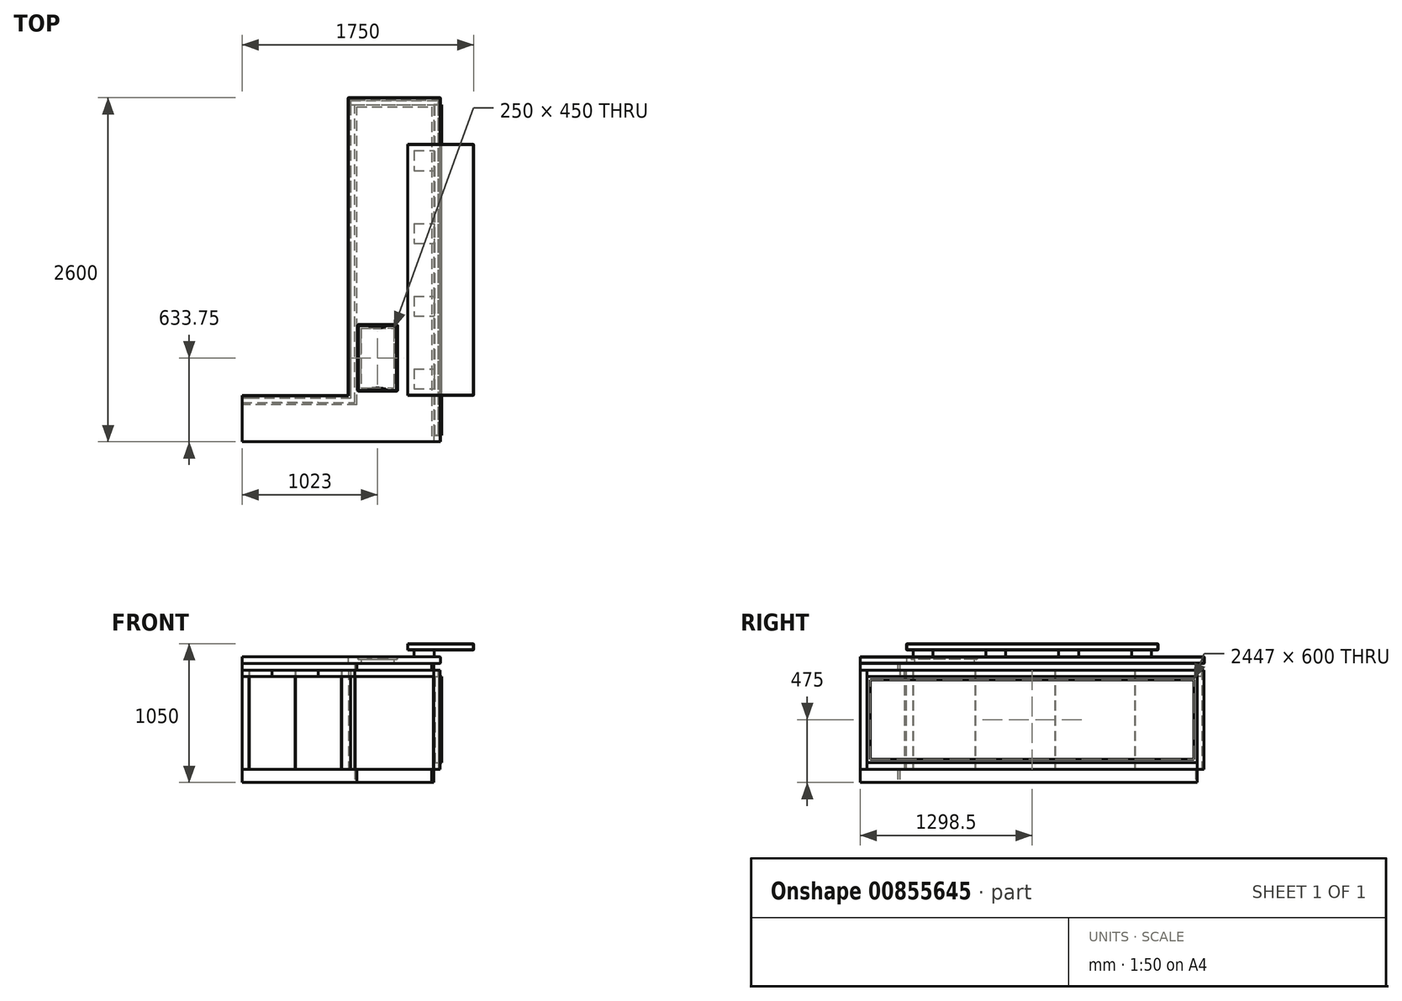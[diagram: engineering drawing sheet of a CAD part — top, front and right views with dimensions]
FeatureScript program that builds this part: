
annotation { "Feature Type Name" : "Feature", "Feature Type Description" : "" }
export const myFeature = defineFeature(function(context is Context, id is Id, definition is map)
    precondition{}
    {
        {
            var Q0;
            Q0=qCreatedBy(makeId("Top.planeOp"),FACE);
            var sketch = newSketch(context, id + "F0", { "sketchPlane" : qUnion([Q0])});
            skLineSegment(sketch, "E0", {"start": v(0, 0) * mm, "end": v(1500, 0) * mm});
            skLineSegment(sketch, "E1", {"start": v(1500, 0) * mm, "end": v(1500, 2600) * mm});
            skLineSegment(sketch, "E2", {"start": v(1500, 2600) * mm, "end": v(800, 2600) * mm});
            skLineSegment(sketch, "E3", {"start": v(800, 2600) * mm, "end": v(800, 350) * mm});
            skLineSegment(sketch, "E4", {"start": v(800, 350) * mm, "end": v(0, 350) * mm});
            skLineSegment(sketch, "E5", {"start": v(0, 350) * mm, "end": v(0, 0) * mm});
            skLineSegment(sketch, "E6.bottom", {"start": v(225, 300) * mm, "end": v(575, 300) * mm});
            skLineSegment(sketch, "E6.top", {"start": v(225, 50) * mm, "end": v(575, 50) * mm});
            skLineSegment(sketch, "E6.left", {"start": v(225, 300) * mm, "end": v(225, 50) * mm});
            skLineSegment(sketch, "E6.right", {"start": v(575, 300) * mm, "end": v(575, 50) * mm});
            skLineSegment(sketch, "E7", {"start": v(400, 350) * mm, "end": v(400, 300) * mm, "construction": true});
            skLineSegment(sketch, "E8", {"start": v(400, 50) * mm, "end": v(400, 0) * mm, "construction": true});
            skSolve(sketch);
        }
        {
            var Q0;
            Q0=makeQuery(id+"F0.imprint","IMPRINT",FACE,{"disambiguationData":[TD([[makeQuery(id+"F0.imprint","IMPRINT",EDGE,{"derivedFrom":sQuery(id+"F0.wireOp",EDGE,"E0")}),1.0]])]});
            var Q1;
            Q1=makeQuery(id+"F0.imprint","IMPRINT",FACE,{"disambiguationData":[TD([[makeQuery(id+"F0.imprint","IMPRINT",EDGE,{"derivedFrom":sQuery(id+"F0.wireOp",EDGE,"E6.bottom")}),-1.0]])]});
            extrude(context, id + "F1", {"entities" : qUnion([Q0, Q1]), "depth" : 950 * mm, "offsetDistance" : 25 * mm, "hasSecondDirection" : true, "secondDirectionOppositeDirection" : false, "secondDirectionDepth" : 900 * mm});
        }
        {
            var Q0;
            Q0=makeQuery(id+"F1.opExtrude","CAP_FACE",FACE,{"disambiguationData":[OSD([sQuery(id+"F0.wireOp",EDGE,"E0"),sQuery(id+"F0.wireOp",EDGE,"E1"),sQuery(id+"F0.wireOp",EDGE,"E2"),sQuery(id+"F0.wireOp",EDGE,"E3"),sQuery(id+"F0.wireOp",EDGE,"E4"),sQuery(id+"F0.wireOp",EDGE,"E5"),sQuery(id+"F0.wireOp",EDGE,"E6.bottom"),sQuery(id+"F0.wireOp",EDGE,"E6.top"),sQuery(id+"F0.wireOp",EDGE,"E6.left"),sQuery(id+"F0.wireOp",EDGE,"E6.right")])],"isStart":false});
            var sketch = newSketch(context, id + "F2", { "sketchPlane" : qUnion([Q0])});
            skLineSegment(sketch, "E9.bottom", {"start": v(1250, 2250) * mm, "end": v(1750, 2250) * mm});
            skLineSegment(sketch, "E9.top", {"start": v(1250, 350) * mm, "end": v(1750, 350) * mm});
            skLineSegment(sketch, "E9.left", {"start": v(1250, 2250) * mm, "end": v(1250, 350) * mm});
            skLineSegment(sketch, "E9.right", {"start": v(1750, 2250) * mm, "end": v(1750, 350) * mm});
            skLineSegment(sketch, "E10", {"start": v(1500, 2600) * mm, "end": v(1500, 2250) * mm, "construction": true});
            skLineSegment(sketch, "E11", {"start": v(1500, 0) * mm, "end": v(1500, 350) * mm, "construction": true});
            skLineSegment(sketch, "E12", {"start": v(800, 350) * mm, "end": v(1250, 350) * mm, "construction": true});
            skLineSegment(sketch, "E13.bottom", {"start": v(1300, 2200) * mm, "end": v(1450, 2200) * mm});
            skLineSegment(sketch, "E13.top", {"start": v(1300, 2050) * mm, "end": v(1450, 2050) * mm});
            skLineSegment(sketch, "E13.left", {"start": v(1300, 2200) * mm, "end": v(1300, 2050) * mm});
            skLineSegment(sketch, "E13.right", {"start": v(1450, 2200) * mm, "end": v(1450, 2050) * mm});
            skLineSegment(sketch, "E14.bottom", {"start": v(1300, 550) * mm, "end": v(1450, 550) * mm});
            skLineSegment(sketch, "E14.top", {"start": v(1300, 400) * mm, "end": v(1450, 400) * mm});
            skLineSegment(sketch, "E14.left", {"start": v(1300, 550) * mm, "end": v(1300, 400) * mm});
            skLineSegment(sketch, "E14.right", {"start": v(1450, 550) * mm, "end": v(1450, 400) * mm});
            skLineSegment(sketch, "E15.bottom", {"start": v(1300, 1650) * mm, "end": v(1450, 1650) * mm});
            skLineSegment(sketch, "E15.top", {"start": v(1300, 1500) * mm, "end": v(1450, 1500) * mm});
            skLineSegment(sketch, "E15.left", {"start": v(1300, 1650) * mm, "end": v(1300, 1500) * mm});
            skLineSegment(sketch, "E15.right", {"start": v(1450, 1650) * mm, "end": v(1450, 1500) * mm});
            skLineSegment(sketch, "E16.bottom", {"start": v(1300, 1100) * mm, "end": v(1450, 1100) * mm});
            skLineSegment(sketch, "E16.top", {"start": v(1300, 950) * mm, "end": v(1450, 950) * mm});
            skLineSegment(sketch, "E16.left", {"start": v(1300, 1100) * mm, "end": v(1300, 950) * mm});
            skLineSegment(sketch, "E16.right", {"start": v(1450, 1100) * mm, "end": v(1450, 950) * mm});
            skLineSegment(sketch, "E17", {"start": v(1500, 2250) * mm, "end": v(1500, 350) * mm, "construction": true});
            skLineSegment(sketch, "E18", {"start": v(1300, 2125) * mm, "end": v(1250, 2125) * mm, "construction": true});
            skLineSegment(sketch, "E19", {"start": v(1450, 2125) * mm, "end": v(1500, 2125) * mm, "construction": true});
            skLineSegment(sketch, "E20", {"start": v(1375, 2200) * mm, "end": v(1375, 2250) * mm, "construction": true});
            skLineSegment(sketch, "E21", {"start": v(1375, 400) * mm, "end": v(1375, 350) * mm, "construction": true});
            skLineSegment(sketch, "E22", {"start": v(1375, 2050) * mm, "end": v(1375, 1650) * mm, "construction": true});
            skLineSegment(sketch, "E23", {"start": v(1375, 1500) * mm, "end": v(1375, 1100) * mm, "construction": true});
            skLineSegment(sketch, "E24", {"start": v(1375, 950) * mm, "end": v(1375, 550) * mm, "construction": true});
            skSolve(sketch);
        }
        {
            var Q0;
            {var subQ0=sQuery(id+"F2.wireOp",EDGE,"E9.right");Q0=makeQuery(id+"F2.imprint","IMPRINT",FACE,{"disambiguationData":[TD([[makeQuery(id+"F2.imprint","IMPRINT",EDGE,{"derivedFrom":subQ0}),-1.0]])]});}
            var Q1;
            {var subQ5=sQuery(id+"F2.wireOp",EDGE,"E9.left");Q1=makeQuery(id+"F2.imprint","IMPRINT",FACE,{"disambiguationData":[TD([[makeQuery(id+"F2.imprint","IMPRINT",EDGE,{"derivedFrom":subQ5}),1.0]])]});}
            var Q2;
            Q2=makeQuery(id+"F2.imprint","IMPRINT",FACE,{"disambiguationData":[TD([[makeQuery(id+"F2.imprint","IMPRINT",EDGE,{"derivedFrom":sQuery(id+"F2.wireOp",EDGE,"E13.bottom")}),-1.0]])]});
            var Q3;
            Q3=makeQuery(id+"F2.imprint","IMPRINT",FACE,{"disambiguationData":[TD([[makeQuery(id+"F2.imprint","IMPRINT",EDGE,{"derivedFrom":sQuery(id+"F2.wireOp",EDGE,"E15.bottom")}),-1.0]])]});
            var Q4;
            Q4=makeQuery(id+"F2.imprint","IMPRINT",FACE,{"disambiguationData":[TD([[makeQuery(id+"F2.imprint","IMPRINT",EDGE,{"derivedFrom":sQuery(id+"F2.wireOp",EDGE,"E16.bottom")}),-1.0]])]});
            var Q5;
            Q5=makeQuery(id+"F2.imprint","IMPRINT",FACE,{"disambiguationData":[TD([[makeQuery(id+"F2.imprint","IMPRINT",EDGE,{"derivedFrom":sQuery(id+"F2.wireOp",EDGE,"E14.bottom")}),-1.0]])]});
            extrude(context, id + "F3", {"entities" : qUnion([Q0, Q1, Q2, Q3, Q4, Q5]), "depth" : 100 * mm, "offsetDistance" : 25 * mm, "hasSecondDirection" : true, "secondDirectionOppositeDirection" : false, "secondDirectionDepth" : 50 * mm});
        }
        {
            var Q0;
            Q0=makeQuery(id+"F2.imprint","IMPRINT",FACE,{"disambiguationData":[TD([[makeQuery(id+"F2.imprint","IMPRINT",EDGE,{"derivedFrom":sQuery(id+"F2.wireOp",EDGE,"E15.bottom")}),-1.0]])]});
            var Q1;
            Q1=makeQuery(id+"F2.imprint","IMPRINT",FACE,{"disambiguationData":[TD([[makeQuery(id+"F2.imprint","IMPRINT",EDGE,{"derivedFrom":sQuery(id+"F2.wireOp",EDGE,"E13.bottom")}),-1.0]])]});
            var Q2;
            Q2=makeQuery(id+"F2.imprint","IMPRINT",FACE,{"disambiguationData":[TD([[makeQuery(id+"F2.imprint","IMPRINT",EDGE,{"derivedFrom":sQuery(id+"F2.wireOp",EDGE,"E16.bottom")}),-1.0]])]});
            var Q3;
            Q3=makeQuery(id+"F2.imprint","IMPRINT",FACE,{"disambiguationData":[TD([[makeQuery(id+"F2.imprint","IMPRINT",EDGE,{"derivedFrom":sQuery(id+"F2.wireOp",EDGE,"E14.bottom")}),-1.0]])]});
            extrude(context, id + "F4", {"entities" : qUnion([Q0, Q1, Q2, Q3]), "depth" : 50 * mm, "offsetDistance" : 25 * mm});
        }
        {
            var Q0;
            Q0=makeQuery(id+"F3.opExtrude","CAP_FACE",FACE,{"disambiguationData":[OSD([sQuery(id+"F2.wireOp",EDGE,"E9.bottom"),sQuery(id+"F2.wireOp",EDGE,"E9.top"),sQuery(id+"F2.wireOp",EDGE,"E9.left"),sQuery(id+"F2.wireOp",EDGE,"E9.right")])],"isStart":false});
            var Q1;
            Q1=makeQuery(id+"F3.opExtrude","CAP_FACE",FACE,{"disambiguationData":[OSD([sQuery(id+"F2.wireOp",EDGE,"E9.bottom"),sQuery(id+"F2.wireOp",EDGE,"E9.top"),sQuery(id+"F2.wireOp",EDGE,"E9.left"),sQuery(id+"F2.wireOp",EDGE,"E9.right")])],"isStart":true});
            var Q2;
            Q2=makeQuery(id+"F3.opExtrude","SWEPT_EDGE",EDGE,{"disambiguationData":[OSD([sQuery(id+"F2.wireOp",EDGE,"E9.bottom"),sQuery(id+"F2.wireOp",EDGE,"E9.right")])]});
            var Q3;
            Q3=makeQuery(id+"F1.opExtrude","SWEPT_EDGE",EDGE,{"disambiguationData":[OSD([sQuery(id+"F0.wireOp",EDGE,"E1"),sQuery(id+"F0.wireOp",EDGE,"E2")])]});
            var Q4;
            Q4=makeQuery(id+"F3.opExtrude","SWEPT_EDGE",EDGE,{"disambiguationData":[OSD([sQuery(id+"F2.wireOp",EDGE,"E9.bottom"),sQuery(id+"F2.wireOp",EDGE,"E9.left")])]});
            var Q5;
            Q5=makeQuery(id+"F3.opExtrude","SWEPT_EDGE",EDGE,{"disambiguationData":[OSD([sQuery(id+"F2.wireOp",EDGE,"E9.top"),sQuery(id+"F2.wireOp",EDGE,"E9.left")])]});
            var Q6;
            Q6=makeQuery(id+"F1.opExtrude","SWEPT_EDGE",EDGE,{"disambiguationData":[OSD([sQuery(id+"F0.wireOp",EDGE,"E2"),sQuery(id+"F0.wireOp",EDGE,"E3")])]});
            var Q7;
            Q7=makeQuery(id+"F3.opExtrude","SWEPT_EDGE",EDGE,{"disambiguationData":[OSD([sQuery(id+"F2.wireOp",EDGE,"E9.top"),sQuery(id+"F2.wireOp",EDGE,"E9.right")])]});
            var Q8;
            Q8=makeQuery(id+"F1.opExtrude","CAP_EDGE",EDGE,{"disambiguationData":[OSD([sQuery(id+"F0.wireOp",EDGE,"E4")])],"isStart":false});
            var Q9;
            Q9=makeQuery(id+"F1.opExtrude","CAP_EDGE",EDGE,{"disambiguationData":[OSD([sQuery(id+"F0.wireOp",EDGE,"E3")])],"isStart":true});
            var Q10;
            Q10=makeQuery(id+"F1.opExtrude","CAP_EDGE",EDGE,{"disambiguationData":[OSD([sQuery(id+"F0.wireOp",EDGE,"E3")])],"isStart":false});
            var Q11;
            Q11=makeQuery(id+"F1.opExtrude","CAP_EDGE",EDGE,{"disambiguationData":[OSD([sQuery(id+"F0.wireOp",EDGE,"E4")])],"isStart":true});
            var Q12;
            Q12=makeQuery(id+"F1.opExtrude","CAP_EDGE",EDGE,{"disambiguationData":[OSD([sQuery(id+"F0.wireOp",EDGE,"E2")])],"isStart":false});
            var Q13;
            Q13=makeQuery(id+"F1.opExtrude","CAP_EDGE",EDGE,{"disambiguationData":[OSD([sQuery(id+"F0.wireOp",EDGE,"E2")])],"isStart":true});
            var Q14;
            Q14=makeQuery(id+"F1.opExtrude","CAP_EDGE",EDGE,{"disambiguationData":[OSD([sQuery(id+"F0.wireOp",EDGE,"E1")])],"isStart":false});
            var Q15;
            Q15=makeQuery(id+"F1.opExtrude","CAP_EDGE",EDGE,{"disambiguationData":[OSD([sQuery(id+"F0.wireOp",EDGE,"E1")])],"isStart":true});
            chamfer(context, id + "F5", {"entities" : qUnion([Q0, Q1, Q2, Q3, Q4, Q5, Q6, Q7, Q8, Q9, Q10, Q11, Q12, Q13, Q14, Q15]), "width" : 3 * mm, "tangentPropagation" : true});
        }
        {
            var Q0;
            Q0=makeQuery(id+"F0.imprint","IMPRINT",FACE,{"disambiguationData":[TD([[makeQuery(id+"F0.imprint","IMPRINT",EDGE,{"derivedFrom":sQuery(id+"F0.wireOp",EDGE,"E0")}),1.0]])]});
            var sketch = newSketch(context, id + "F6", { "sketchPlane" : qUnion([Q0])});
            skLineSegment(sketch, "E25.bottom", {"start": v(0, 347) * mm, "end": v(50, 347) * mm});
            skLineSegment(sketch, "E25.top", {"start": v(0, 332) * mm, "end": v(50, 332) * mm});
            skLineSegment(sketch, "E25.left", {"start": v(0, 347) * mm, "end": v(0, 332) * mm});
            skLineSegment(sketch, "E25.right", {"start": v(50, 347) * mm, "end": v(50, 332) * mm});
            skLineSegment(sketch, "E26.bottom", {"start": v(753, 347) * mm, "end": v(803, 347) * mm});
            skLineSegment(sketch, "E26.top", {"start": v(753, 332) * mm, "end": v(803, 332) * mm});
            skLineSegment(sketch, "E26.left", {"start": v(753, 347) * mm, "end": v(753, 332) * mm});
            skLineSegment(sketch, "E26.right", {"start": v(803, 347) * mm, "end": v(803, 332) * mm});
            skLineSegment(sketch, "E27.bottom", {"start": v(803, 397) * mm, "end": v(818, 397) * mm});
            skLineSegment(sketch, "E27.top", {"start": v(803, 347) * mm, "end": v(818, 347) * mm});
            skLineSegment(sketch, "E27.left", {"start": v(803, 397) * mm, "end": v(803, 347) * mm});
            skLineSegment(sketch, "E27.right", {"start": v(818, 397) * mm, "end": v(818, 347) * mm});
            skLineSegment(sketch, "E28.bottom", {"start": v(803, 2597) * mm, "end": v(818, 2597) * mm});
            skLineSegment(sketch, "E28.top", {"start": v(803, 2547) * mm, "end": v(818, 2547) * mm});
            skLineSegment(sketch, "E28.left", {"start": v(803, 2597) * mm, "end": v(803, 2547) * mm});
            skLineSegment(sketch, "E28.right", {"start": v(818, 2597) * mm, "end": v(818, 2547) * mm});
            skLineSegment(sketch, "E29", {"start": v(50, 347) * mm, "end": v(50, 350) * mm});
            skLineSegment(sketch, "E30", {"start": v(753, 347) * mm, "end": v(753, 350) * mm});
            skLineSegment(sketch, "E31", {"start": v(803, 397) * mm, "end": v(800, 397) * mm});
            skLineSegment(sketch, "E32.bottom", {"start": v(53, 347) * mm, "end": v(400, 347) * mm});
            skLineSegment(sketch, "E32.top", {"start": v(53, 332) * mm, "end": v(400, 332) * mm});
            skLineSegment(sketch, "E32.left", {"start": v(53, 347) * mm, "end": v(53, 332) * mm});
            skLineSegment(sketch, "E32.right", {"start": v(400, 347) * mm, "end": v(400, 332) * mm});
            skLineSegment(sketch, "E33.bottom", {"start": v(403, 347) * mm, "end": v(750, 347) * mm});
            skLineSegment(sketch, "E33.top", {"start": v(403, 332) * mm, "end": v(750, 332) * mm});
            skLineSegment(sketch, "E33.left", {"start": v(403, 347) * mm, "end": v(403, 332) * mm});
            skLineSegment(sketch, "E33.right", {"start": v(750, 347) * mm, "end": v(750, 332) * mm});
            skLineSegment(sketch, "E34", {"start": v(753, 347) * mm, "end": v(750, 347) * mm});
            skLineSegment(sketch, "E35", {"start": v(400, 347) * mm, "end": v(403, 347) * mm});
            skLineSegment(sketch, "E36", {"start": v(53, 347) * mm, "end": v(50, 347) * mm});
            skLineSegment(sketch, "E37.bottom", {"start": v(803, 2073.5) * mm, "end": v(818, 2073.5) * mm});
            skLineSegment(sketch, "E37.top", {"start": v(803, 1473.5) * mm, "end": v(818, 1473.5) * mm});
            skLineSegment(sketch, "E37.left", {"start": v(803, 2073.5) * mm, "end": v(803, 1473.5) * mm});
            skLineSegment(sketch, "E37.right", {"start": v(818, 2073.5) * mm, "end": v(818, 1473.5) * mm});
            skLineSegment(sketch, "E38.bottom", {"start": v(803, 1470.5) * mm, "end": v(818, 1470.5) * mm});
            skLineSegment(sketch, "E38.top", {"start": v(803, 870.5) * mm, "end": v(818, 870.5) * mm});
            skLineSegment(sketch, "E38.left", {"start": v(803, 1470.5) * mm, "end": v(803, 870.5) * mm});
            skLineSegment(sketch, "E38.right", {"start": v(818, 1470.5) * mm, "end": v(818, 870.5) * mm});
            skLineSegment(sketch, "E39.bottom", {"start": v(803, 867.5) * mm, "end": v(818, 867.5) * mm});
            skLineSegment(sketch, "E39.top", {"start": v(803, 400) * mm, "end": v(818, 400) * mm});
            skLineSegment(sketch, "E39.left", {"start": v(803, 867.5) * mm, "end": v(803, 400) * mm});
            skLineSegment(sketch, "E39.right", {"start": v(818, 867.5) * mm, "end": v(818, 400) * mm});
            skLineSegment(sketch, "E40.bottom", {"start": v(803, 2544) * mm, "end": v(818, 2544) * mm});
            skLineSegment(sketch, "E40.top", {"start": v(803, 2076.5) * mm, "end": v(818, 2076.5) * mm});
            skLineSegment(sketch, "E40.left", {"start": v(803, 2544) * mm, "end": v(803, 2076.5) * mm});
            skLineSegment(sketch, "E40.right", {"start": v(818, 2544) * mm, "end": v(818, 2076.5) * mm});
            skLineSegment(sketch, "E41", {"start": v(803, 2547) * mm, "end": v(803, 2544) * mm});
            skLineSegment(sketch, "E42", {"start": v(803, 2076.5) * mm, "end": v(803, 2073.5) * mm});
            skLineSegment(sketch, "E43", {"start": v(803, 867.5) * mm, "end": v(803, 870.5) * mm});
            skLineSegment(sketch, "E44", {"start": v(803, 1473.5) * mm, "end": v(803, 1470.5) * mm});
            skLineSegment(sketch, "E45", {"start": v(803, 400) * mm, "end": v(803, 397) * mm});
            skLineSegment(sketch, "E46", {"start": v(803, 2597) * mm, "end": v(803, 2600) * mm});
            skLineSegment(sketch, "E47", {"start": v(818, 2597) * mm, "end": v(1497, 2597) * mm});
            skLineSegment(sketch, "E48", {"start": v(1497, 2597) * mm, "end": v(1497, 0) * mm});
            skLineSegment(sketch, "E49", {"start": v(1497, 2597) * mm, "end": v(1500, 2597) * mm});
            skLineSegment(sketch, "E50.bottom", {"start": v(0, 297) * mm, "end": v(853, 297) * mm});
            skLineSegment(sketch, "E50.top", {"start": v(0, 282) * mm, "end": v(853, 282) * mm});
            skLineSegment(sketch, "E50.left", {"start": v(0, 297) * mm, "end": v(0, 282) * mm});
            skLineSegment(sketch, "E50.right", {"start": v(853, 297) * mm, "end": v(853, 282) * mm});
            skLineSegment(sketch, "E51.bottom", {"start": v(853, 297) * mm, "end": v(868, 297) * mm});
            skLineSegment(sketch, "E51.top", {"start": v(853, 2532) * mm, "end": v(868, 2532) * mm});
            skLineSegment(sketch, "E51.left", {"start": v(853, 297) * mm, "end": v(853, 2532) * mm});
            skLineSegment(sketch, "E51.right", {"start": v(868, 297) * mm, "end": v(868, 2532) * mm});
            skLineSegment(sketch, "E52.bottom", {"start": v(868, 2532) * mm, "end": v(1432, 2532) * mm});
            skLineSegment(sketch, "E52.top", {"start": v(868, 2547) * mm, "end": v(1432, 2547) * mm});
            skLineSegment(sketch, "E52.left", {"start": v(868, 2532) * mm, "end": v(868, 2547) * mm});
            skLineSegment(sketch, "E52.right", {"start": v(1432, 2532) * mm, "end": v(1432, 2547) * mm});
            skLineSegment(sketch, "E53.bottom", {"start": v(1432, 2532) * mm, "end": v(1447, 2532) * mm});
            skLineSegment(sketch, "E53.top", {"start": v(1432, 0) * mm, "end": v(1447, 0) * mm});
            skLineSegment(sketch, "E53.left", {"start": v(1432, 2532) * mm, "end": v(1432, 0) * mm});
            skLineSegment(sketch, "E53.right", {"start": v(1447, 2532) * mm, "end": v(1447, 0) * mm});
            skLineSegment(sketch, "E54", {"start": v(868, 2547) * mm, "end": v(853, 2547) * mm});
            skLineSegment(sketch, "E55", {"start": v(853, 2547) * mm, "end": v(853, 2532) * mm});
            skLineSegment(sketch, "E56", {"start": v(1432, 2547) * mm, "end": v(1447, 2547) * mm});
            skLineSegment(sketch, "E57", {"start": v(1447, 2547) * mm, "end": v(1447, 2532) * mm});
            skLineSegment(sketch, "E58", {"start": v(818, 347) * mm, "end": v(818, 332) * mm});
            skLineSegment(sketch, "E59", {"start": v(818, 332) * mm, "end": v(803, 332) * mm});
            skLineSegment(sketch, "E60", {"start": v(868, 297) * mm, "end": v(868, 282) * mm});
            skLineSegment(sketch, "E61", {"start": v(868, 282) * mm, "end": v(853, 282) * mm});
            skLineSegment(sketch, "E62", {"start": v(818, 2547) * mm, "end": v(853, 2547) * mm});
            skLineSegment(sketch, "E63", {"start": v(821, 2547) * mm, "end": v(821, 329) * mm});
            skLineSegment(sketch, "E64", {"start": v(821, 329) * mm, "end": v(0, 329) * mm});
            skLineSegment(sketch, "E65", {"start": v(0, 332) * mm, "end": v(0, 297) * mm});
            skLineSegment(sketch, "E66", {"start": v(818, 397) * mm, "end": v(821, 397) * mm});
            skLineSegment(sketch, "E67", {"start": v(753, 332) * mm, "end": v(753, 329) * mm});
            skLineSegment(sketch, "E68", {"start": v(803, 2597) * mm, "end": v(853, 2597) * mm});
            skLineSegment(sketch, "E69", {"start": v(853, 2597) * mm, "end": v(853, 2582) * mm});
            skLineSegment(sketch, "E70", {"start": v(853, 2582) * mm, "end": v(818, 2582) * mm});
            skLineSegment(sketch, "E71", {"start": v(856, 2597) * mm, "end": v(856, 2582) * mm});
            skLineSegment(sketch, "E72", {"start": v(856, 2582) * mm, "end": v(1444, 2582) * mm});
            skLineSegment(sketch, "E73", {"start": v(1444, 2582) * mm, "end": v(1444, 2597) * mm});
            skLineSegment(sketch, "E74", {"start": v(1447, 2597) * mm, "end": v(1447, 2582) * mm});
            skLineSegment(sketch, "E75", {"start": v(1447, 2582) * mm, "end": v(1482, 2582) * mm});
            skLineSegment(sketch, "E76", {"start": v(1482, 2582) * mm, "end": v(1482, 2547) * mm});
            skLineSegment(sketch, "E77", {"start": v(1482, 2547) * mm, "end": v(1497, 2547) * mm});
            skLineSegment(sketch, "E78", {"start": v(856, 2582) * mm, "end": v(853, 2582) * mm});
            skLineSegment(sketch, "E79", {"start": v(1447, 2582) * mm, "end": v(1444, 2582) * mm});
            skLineSegment(sketch, "E80", {"start": v(1497, 0) * mm, "end": v(1482, 0) * mm});
            skLineSegment(sketch, "E81", {"start": v(1482, 0) * mm, "end": v(1482, 50) * mm});
            skLineSegment(sketch, "E82", {"start": v(1482, 50) * mm, "end": v(1497, 50) * mm});
            skLineSegment(sketch, "E83", {"start": v(821, 2547) * mm, "end": v(821, 2579) * mm});
            skLineSegment(sketch, "E84", {"start": v(821, 2579) * mm, "end": v(1479, 2579) * mm});
            skLineSegment(sketch, "E85", {"start": v(1479, 2579) * mm, "end": v(1479, 2547) * mm});
            skLineSegment(sketch, "E86", {"start": v(1479, 2547) * mm, "end": v(1447, 2547) * mm});
            skLineSegment(sketch, "E87", {"start": v(1482, 2547) * mm, "end": v(1479, 2547) * mm});
            skLineSegment(sketch, "E88", {"start": v(1447, 2582) * mm, "end": v(1447, 2579) * mm});
            skLineSegment(sketch, "E89", {"start": v(1482, 50) * mm, "end": v(1447, 50) * mm});
            skLineSegment(sketch, "E90", {"start": v(1482, 0) * mm, "end": v(1447, 0) * mm});
            skLineSegment(sketch, "E91.bottom", {"start": v(873, 883.75) * mm, "end": v(1173, 883.75) * mm});
            skLineSegment(sketch, "E91.top", {"start": v(873, 383.75) * mm, "end": v(1173, 383.75) * mm});
            skLineSegment(sketch, "E91.left", {"start": v(873, 883.75) * mm, "end": v(873, 383.75) * mm});
            skLineSegment(sketch, "E91.right", {"start": v(1173, 883.75) * mm, "end": v(1173, 383.75) * mm});
            skLineSegment(sketch, "E92", {"start": v(818, 633.75) * mm, "end": v(873, 633.75) * mm, "construction": true});
            skLineSegment(sketch, "E93.bottom", {"start": v(876, 880.75) * mm, "end": v(1170, 880.75) * mm});
            skLineSegment(sketch, "E93.top", {"start": v(876, 386.75) * mm, "end": v(1170, 386.75) * mm});
            skLineSegment(sketch, "E93.left", {"start": v(876, 880.75) * mm, "end": v(876, 386.75) * mm});
            skLineSegment(sketch, "E93.right", {"start": v(1170, 880.75) * mm, "end": v(1170, 386.75) * mm});
            skLineSegment(sketch, "E94", {"start": v(1023, 883.75) * mm, "end": v(1023, 880.75) * mm});
            skPoint(sketch, "E94.endSnap0", {"position": v(1023, 880.75) * mm});
            skLineSegment(sketch, "E95", {"start": v(1173, 633.75) * mm, "end": v(1170, 633.75) * mm});
            skLineSegment(sketch, "E96", {"start": v(876, 880.75) * mm, "end": v(948, 880.75) * mm});
            skLineSegment(sketch, "E97", {"start": v(948, 880.75) * mm, "end": v(1098, 880.75) * mm, "construction": true});
            skLineSegment(sketch, "E98", {"start": v(1098, 880.75) * mm, "end": v(1170, 880.75) * mm});
            skArc(sketch, "E99", {"start": v(948, 880.75) * mm, "mid": v(1023, 863.75) * mm, "end": v(1098, 880.75) * mm});
            skLineSegment(sketch, "E100", {"start": v(1023, 880.75) * mm, "end": v(1023, 863.75) * mm});
            skLineSegment(sketch, "E101", {"start": v(876, 386.75) * mm, "end": v(948, 386.75) * mm});
            skLineSegment(sketch, "E102", {"start": v(948, 386.75) * mm, "end": v(1098, 386.75) * mm});
            skLineSegment(sketch, "E103", {"start": v(1098, 386.75) * mm, "end": v(1170, 386.75) * mm});
            skArc(sketch, "E104", {"start": v(1098, 386.75) * mm, "mid": v(1023, 403.75) * mm, "end": v(948, 386.75) * mm});
            skLineSegment(sketch, "E105.bottom", {"start": v(898, 858.75) * mm, "end": v(1148, 858.75) * mm});
            skLineSegment(sketch, "E105.top", {"start": v(898, 408.75) * mm, "end": v(1148, 408.75) * mm});
            skLineSegment(sketch, "E105.left", {"start": v(898, 858.75) * mm, "end": v(898, 408.75) * mm});
            skLineSegment(sketch, "E105.right", {"start": v(1148, 858.75) * mm, "end": v(1148, 408.75) * mm});
            skLineSegment(sketch, "E106", {"start": v(1173, 633.75) * mm, "end": v(1148, 633.75) * mm, "construction": true});
            skLineSegment(sketch, "E107", {"start": v(1023, 883.75) * mm, "end": v(1023, 858.75) * mm, "construction": true});
            skLineSegment(sketch, "E108.bottom", {"start": v(923, 833.75) * mm, "end": v(1123, 833.75) * mm});
            skLineSegment(sketch, "E108.top", {"start": v(923, 533.75) * mm, "end": v(1123, 533.75) * mm});
            skLineSegment(sketch, "E108.left", {"start": v(923, 833.75) * mm, "end": v(923, 533.75) * mm});
            skLineSegment(sketch, "E108.right", {"start": v(1123, 833.75) * mm, "end": v(1123, 533.75) * mm});
            skLineSegment(sketch, "E109", {"start": v(1023, 858.75) * mm, "end": v(1023, 833.75) * mm, "construction": true});
            skLineSegment(sketch, "E110", {"start": v(1123, 833.75) * mm, "end": v(1148, 833.75) * mm, "construction": true});
            skLineSegment(sketch, "E111", {"start": v(1098, 533.75) * mm, "end": v(1098, 471.25) * mm, "construction": true});
            skLineSegment(sketch, "E112", {"start": v(1098, 471.25) * mm, "end": v(1098, 408.75) * mm, "construction": true});
            skCircle(sketch, "E113", {"center": v(1098, 471.25) * mm, "radius": 25 * mm});
            skSolve(sketch);
        }
        {
            var Q0;
            Q0=makeQuery(id+"F6.imprint","IMPRINT",FACE,{"disambiguationData":[TD([[makeQuery(id+"F6.imprint","IMPRINT",EDGE,{"derivedFrom":sQuery(id+"F6.wireOp",EDGE,"E52.bottom")}),1.0]])]});
            var Q1;
            Q1=makeQuery(id+"F6.imprint","IMPRINT",FACE,{"disambiguationData":[TD([[makeQuery(id+"F6.imprint","IMPRINT",EDGE,{"derivedFrom":sQuery(id+"F6.wireOp",EDGE,"E53.bottom")}),-1.0]])]});
            var Q2;
            Q2=makeQuery(id+"F6.imprint","IMPRINT",FACE,{"disambiguationData":[TD([[makeQuery(id+"F6.imprint","IMPRINT",EDGE,{"derivedFrom":sQuery(id+"F6.wireOp",EDGE,"E52.right")}),-1.0]])]});
            var Q3;
            Q3=makeQuery(id+"F6.imprint","IMPRINT",FACE,{"disambiguationData":[TD([[makeQuery(id+"F6.imprint","IMPRINT",EDGE,{"derivedFrom":sQuery(id+"F6.wireOp",EDGE,"E51.bottom")}),1.0]])]});
            var Q4;
            Q4=makeQuery(id+"F6.imprint","IMPRINT",FACE,{"disambiguationData":[TD([[makeQuery(id+"F6.imprint","IMPRINT",EDGE,{"derivedFrom":sQuery(id+"F6.wireOp",EDGE,"E51.top")}),1.0]])]});
            var Q5;
            Q5=makeQuery(id+"F6.imprint","IMPRINT",FACE,{"disambiguationData":[TD([[makeQuery(id+"F6.imprint","IMPRINT",EDGE,{"derivedFrom":sQuery(id+"F6.wireOp",EDGE,"E50.right")}),1.0]])]});
            var Q6;
            {var subQ0=sQuery(id+"F6.wireOp",EDGE,"E50.right");Q6=makeQuery(id+"F6.imprint","IMPRINT",FACE,{"disambiguationData":[TD([[makeQuery(id+"F6.imprint","IMPRINT",EDGE,{"derivedFrom":subQ0}),-1.0]])]});}
            var Q7;
            {var subQ0=sQuery(id+"F6.wireOp",EDGE,"E50.bottom");var subQ1=makeQuery(id+"F0.imprint","IMPRINT",EDGE,{"derivedFrom":sQuery(id+"F0.wireOp",EDGE,"E6.left")});var subQ2=makeQuery(id+"F6.imprint","INTERSECT",VERTEX,{"derivedFrom":[subQ1,subQ0]});Q7=makeQuery(id+"F6.imprint","IMPRINT",FACE,{"disambiguationData":[TD([[makeQuery(id+"F6.imprint","IMPRINT",EDGE,{"disambiguationData":[TD([[subQ2,-1.0]])],"derivedFrom":subQ0}),-1.0]])]});}
            var Q8;
            {var subQ0=sQuery(id+"F6.wireOp",EDGE,"E50.left");Q8=makeQuery(id+"F6.imprint","IMPRINT",FACE,{"disambiguationData":[TD([[makeQuery(id+"F6.imprint","IMPRINT",EDGE,{"derivedFrom":subQ0}),1.0]])]});}
            extrude(context, id + "F7", {"entities" : qUnion([Q0, Q1, Q2, Q3, Q4, Q5, Q6, Q7, Q8]), "depth" : 100 * mm, "offsetDistance" : 25 * mm});
        }
        {
            var Q0;
            Q0=makeQuery(id+"F6.imprint","IMPRINT",FACE,{"disambiguationData":[TD([[makeQuery(id+"F6.imprint","IMPRINT",EDGE,{"derivedFrom":sQuery(id+"F6.wireOp",EDGE,"E25.bottom")}),-1.0]])]});
            var Q1;
            Q1=makeQuery(id+"F6.imprint","IMPRINT",FACE,{"disambiguationData":[TD([[makeQuery(id+"F6.imprint","IMPRINT",EDGE,{"derivedFrom":sQuery(id+"F6.wireOp",EDGE,"E32.bottom")}),-1.0]])]});
            var Q2;
            Q2=makeQuery(id+"F6.imprint","IMPRINT",FACE,{"disambiguationData":[TD([[makeQuery(id+"F6.imprint","IMPRINT",EDGE,{"derivedFrom":sQuery(id+"F6.wireOp",EDGE,"E33.bottom")}),-1.0]])]});
            var Q3;
            Q3=makeQuery(id+"F6.imprint","IMPRINT",FACE,{"disambiguationData":[TD([[makeQuery(id+"F6.imprint","IMPRINT",EDGE,{"derivedFrom":sQuery(id+"F6.wireOp",EDGE,"E26.bottom")}),-1.0]])]});
            var Q4;
            Q4=makeQuery(id+"F6.imprint","IMPRINT",FACE,{"disambiguationData":[TD([[makeQuery(id+"F6.imprint","IMPRINT",EDGE,{"derivedFrom":sQuery(id+"F6.wireOp",EDGE,"E26.right")}),1.0]])]});
            var Q5;
            Q5=makeQuery(id+"F6.imprint","IMPRINT",FACE,{"disambiguationData":[TD([[makeQuery(id+"F6.imprint","IMPRINT",EDGE,{"derivedFrom":sQuery(id+"F6.wireOp",EDGE,"E27.bottom")}),-1.0]])]});
            var Q6;
            Q6=makeQuery(id+"F6.imprint","IMPRINT",FACE,{"disambiguationData":[TD([[makeQuery(id+"F6.imprint","IMPRINT",EDGE,{"derivedFrom":sQuery(id+"F6.wireOp",EDGE,"E39.bottom")}),-1.0]])]});
            var Q7;
            Q7=makeQuery(id+"F6.imprint","IMPRINT",FACE,{"disambiguationData":[TD([[makeQuery(id+"F6.imprint","IMPRINT",EDGE,{"derivedFrom":sQuery(id+"F6.wireOp",EDGE,"E38.bottom")}),-1.0]])]});
            var Q8;
            Q8=makeQuery(id+"F6.imprint","IMPRINT",FACE,{"disambiguationData":[TD([[makeQuery(id+"F6.imprint","IMPRINT",EDGE,{"derivedFrom":sQuery(id+"F6.wireOp",EDGE,"E37.bottom")}),-1.0]])]});
            var Q9;
            Q9=makeQuery(id+"F6.imprint","IMPRINT",FACE,{"disambiguationData":[TD([[makeQuery(id+"F6.imprint","IMPRINT",EDGE,{"derivedFrom":sQuery(id+"F6.wireOp",EDGE,"E40.bottom")}),-1.0]])]});
            var Q10;
            Q10=makeQuery(id+"F6.imprint","IMPRINT",FACE,{"disambiguationData":[TD([[makeQuery(id+"F6.imprint","IMPRINT",EDGE,{"derivedFrom":sQuery(id+"F6.wireOp",EDGE,"E28.bottom")}),-1.0]])]});
            extrude(context, id + "F8", {"entities" : qUnion([Q0, Q1, Q2, Q3, Q4, Q5, Q6, Q7, Q8, Q9, Q10]), "depth" : 850 * mm, "offsetDistance" : 25 * mm, "hasSecondDirection" : true, "secondDirectionOppositeDirection" : false, "secondDirectionDepth" : 100 * mm});
        }
        {
            var Q0;
            Q0=makeQuery(id+"F6.imprint","IMPRINT",FACE,{"disambiguationData":[TD([[makeQuery(id+"F6.imprint","IMPRINT",EDGE,{"derivedFrom":sQuery(id+"F6.wireOp",EDGE,"E52.bottom")}),1.0]])]});
            var Q1;
            Q1=makeQuery(id+"F6.imprint","IMPRINT",FACE,{"disambiguationData":[TD([[makeQuery(id+"F6.imprint","IMPRINT",EDGE,{"derivedFrom":sQuery(id+"F6.wireOp",EDGE,"E52.right")}),-1.0]])]});
            var Q2;
            Q2=makeQuery(id+"F6.imprint","IMPRINT",FACE,{"disambiguationData":[TD([[makeQuery(id+"F6.imprint","IMPRINT",EDGE,{"derivedFrom":sQuery(id+"F6.wireOp",EDGE,"E53.bottom")}),-1.0]])]});
            var Q3;
            Q3=makeQuery(id+"F6.imprint","IMPRINT",FACE,{"disambiguationData":[TD([[makeQuery(id+"F6.imprint","IMPRINT",EDGE,{"derivedFrom":sQuery(id+"F6.wireOp",EDGE,"E51.top")}),1.0]])]});
            var Q4;
            Q4=makeQuery(id+"F6.imprint","IMPRINT",FACE,{"disambiguationData":[TD([[makeQuery(id+"F6.imprint","IMPRINT",EDGE,{"derivedFrom":sQuery(id+"F6.wireOp",EDGE,"E51.bottom")}),1.0]])]});
            var Q5;
            Q5=makeQuery(id+"F6.imprint","IMPRINT",FACE,{"disambiguationData":[TD([[makeQuery(id+"F6.imprint","IMPRINT",EDGE,{"derivedFrom":sQuery(id+"F6.wireOp",EDGE,"E50.right")}),1.0]])]});
            var Q6;
            {var subQ0=sQuery(id+"F6.wireOp",EDGE,"E50.right");Q6=makeQuery(id+"F6.imprint","IMPRINT",FACE,{"disambiguationData":[TD([[makeQuery(id+"F6.imprint","IMPRINT",EDGE,{"derivedFrom":subQ0}),-1.0]])]});}
            var Q7;
            {var subQ0=sQuery(id+"F6.wireOp",EDGE,"E50.bottom");var subQ1=makeQuery(id+"F0.imprint","IMPRINT",EDGE,{"derivedFrom":sQuery(id+"F0.wireOp",EDGE,"E6.left")});var subQ2=makeQuery(id+"F6.imprint","INTERSECT",VERTEX,{"derivedFrom":[subQ1,subQ0]});Q7=makeQuery(id+"F6.imprint","IMPRINT",FACE,{"disambiguationData":[TD([[makeQuery(id+"F6.imprint","IMPRINT",EDGE,{"disambiguationData":[TD([[subQ2,-1.0]])],"derivedFrom":subQ0}),-1.0]])]});}
            var Q8;
            {var subQ0=sQuery(id+"F6.wireOp",EDGE,"E50.left");Q8=makeQuery(id+"F6.imprint","IMPRINT",FACE,{"disambiguationData":[TD([[makeQuery(id+"F6.imprint","IMPRINT",EDGE,{"derivedFrom":subQ0}),1.0]])]});}
            extrude(context, id + "F9", {"entities" : qUnion([Q0, Q1, Q2, Q3, Q4, Q5, Q6, Q7, Q8]), "depth" : 900 * mm, "offsetDistance" : 25 * mm, "hasSecondDirection" : true, "secondDirectionOppositeDirection" : false, "secondDirectionDepth" : 850 * mm});
        }
        {
            var Q0;
            {var subQ14=sQuery(id+"F6.wireOp",EDGE,"E51.left");Q0=makeQuery(id+"F6.imprint","IMPRINT",FACE,{"disambiguationData":[TD([[makeQuery(id+"F6.imprint","IMPRINT",EDGE,{"derivedFrom":subQ14}),1.0]])]});}
            extrude(context, id + "F10", {"entities" : qUnion([Q0]), "depth" : 850 * mm, "offsetDistance" : 25 * mm, "hasSecondDirection" : true, "secondDirectionOppositeDirection" : false, "secondDirectionDepth" : 800 * mm});
        }
        {
            var Q0;
            {var subQ1=sQuery(id+"F6.wireOp",EDGE,"E28.top");Q0=makeQuery(id+"F6.imprint","IMPRINT",FACE,{"disambiguationData":[TD([[makeQuery(id+"F6.imprint","IMPRINT",EDGE,{"derivedFrom":subQ1}),1.0]])]});}
            var Q1;
            {var subQ4=sQuery(id+"F6.wireOp",EDGE,"E69");Q1=makeQuery(id+"F6.imprint","IMPRINT",FACE,{"disambiguationData":[TD([[makeQuery(id+"F6.imprint","IMPRINT",EDGE,{"derivedFrom":subQ4}),-1.0]])]});}
            var Q2;
            {var subQ0=sQuery(id+"F6.wireOp",EDGE,"E71");Q2=makeQuery(id+"F6.imprint","IMPRINT",FACE,{"disambiguationData":[TD([[makeQuery(id+"F6.imprint","IMPRINT",EDGE,{"derivedFrom":subQ0}),1.0]])]});}
            var Q3;
            {var subQ0=sQuery(id+"F6.wireOp",EDGE,"E74");Q3=makeQuery(id+"F6.imprint","IMPRINT",FACE,{"disambiguationData":[TD([[makeQuery(id+"F6.imprint","IMPRINT",EDGE,{"derivedFrom":subQ0}),1.0]])]});}
            extrude(context, id + "F11", {"entities" : qUnion([Q0, Q1, Q2, Q3]), "depth" : 850 * mm, "offsetDistance" : 25 * mm, "hasSecondDirection" : true, "secondDirectionOppositeDirection" : false, "secondDirectionDepth" : 100 * mm});
        }
        {
            var Q0;
            {var subQ1=sQuery(id+"F6.wireOp",EDGE,"E57");Q0=makeQuery(id+"F6.imprint","IMPRINT",FACE,{"disambiguationData":[TD([[makeQuery(id+"F6.imprint","IMPRINT",EDGE,{"derivedFrom":subQ1}),1.0]])]});}
            extrude(context, id + "F12", {"entities" : qUnion([Q0]), "depth" : 850 * mm, "offsetDistance" : 25 * mm, "hasSecondDirection" : true, "secondDirectionOppositeDirection" : false, "secondDirectionDepth" : 100 * mm});
        }
        {
            var Q0;
            Q0=makeQuery(id+"F6.imprint","IMPRINT",FACE,{"disambiguationData":[TD([[makeQuery(id+"F6.imprint","IMPRINT",EDGE,{"derivedFrom":sQuery(id+"F6.wireOp",EDGE,"E81")}),1.0]])]});
            var Q1;
            {var subQ0=sQuery(id+"F6.wireOp",EDGE,"E80");Q1=makeQuery(id+"F6.imprint","IMPRINT",FACE,{"disambiguationData":[TD([[makeQuery(id+"F6.imprint","IMPRINT",EDGE,{"derivedFrom":subQ0}),1.0]])]});}
            extrude(context, id + "F13", {"entities" : qUnion([Q0, Q1]), "depth" : 850 * mm, "offsetDistance" : 25 * mm, "hasSecondDirection" : true, "secondDirectionOppositeDirection" : false, "secondDirectionDepth" : 100 * mm});
        }
        {
            var Q0;
            Q0=makeQuery(id+"F6.imprint","IMPRINT",FACE,{"disambiguationData":[TD([[makeQuery(id+"F6.imprint","IMPRINT",EDGE,{"derivedFrom":sQuery(id+"F6.wireOp",EDGE,"E52.top")}),1.0]])]});
            extrude(context, id + "F14", {"entities" : qUnion([Q0]), "depth" : 850 * mm, "offsetDistance" : 25 * mm, "hasSecondDirection" : true, "secondDirectionOppositeDirection" : false, "secondDirectionDepth" : 800 * mm});
        }
        {
            var Q0;
            Q0=makeQuery(id+"F12.opExtrude","SWEPT_FACE",FACE,{"disambiguationData":[OSD([sQuery(id+"F6.wireOp",EDGE,"E48")])]});
            var sketch = newSketch(context, id + "F15", { "sketchPlane" : qUnion([Q0])});
            skLineSegment(sketch, "E114.bottom", {"start": v(50, 800) * mm, "end": v(2547, 800) * mm});
            skLineSegment(sketch, "E114.top", {"start": v(50, 150) * mm, "end": v(2547, 150) * mm});
            skLineSegment(sketch, "E114.left", {"start": v(50, 800) * mm, "end": v(50, 150) * mm});
            skLineSegment(sketch, "E114.right", {"start": v(2547, 800) * mm, "end": v(2547, 150) * mm});
            skLineSegment(sketch, "E115.bottom", {"start": v(75, 775) * mm, "end": v(2522, 775) * mm});
            skLineSegment(sketch, "E115.top", {"start": v(75, 175) * mm, "end": v(2522, 175) * mm});
            skLineSegment(sketch, "E115.left", {"start": v(75, 775) * mm, "end": v(75, 175) * mm});
            skLineSegment(sketch, "E115.right", {"start": v(2522, 775) * mm, "end": v(2522, 175) * mm});
            skLineSegment(sketch, "E116", {"start": v(1298.5, 800) * mm, "end": v(1298.5, 775) * mm, "construction": true});
            skLineSegment(sketch, "E117", {"start": v(75, 475) * mm, "end": v(50, 475) * mm, "construction": true});
            skLineSegment(sketch, "E118", {"start": v(1298.5, 850) * mm, "end": v(1298.5, 800) * mm, "construction": true});
            skLineSegment(sketch, "E119", {"start": v(1298.5, 150) * mm, "end": v(1298.5, 100) * mm, "construction": true});
            skSolve(sketch);
        }
        {
            var Q0;
            Q0=makeQuery(id+"F15.imprint","IMPRINT",FACE,{"disambiguationData":[TD([[makeQuery(id+"F15.imprint","IMPRINT",EDGE,{"derivedFrom":sQuery(id+"F15.wireOp",EDGE,"E114.bottom")}),-1.0]])]});
            var Q1;
            Q1=makeQuery(id+"F15.imprint","IMPRINT",FACE,{"disambiguationData":[TD([[makeQuery(id+"F15.imprint","IMPRINT",EDGE,{"derivedFrom":sQuery(id+"F15.wireOp",EDGE,"E115.bottom")}),-1.0]])]});
            extrude(context, id + "F16", {"entities" : qUnion([Q0, Q1]), "operationType" : NewBodyOperationType.REMOVE, "oppositeDirection" : true, "depth" : 45 * mm, "offsetDistance" : 25 * mm});
        }
        {
            var Q0;
            Q0=makeQuery(id+"F15.imprint","IMPRINT",FACE,{"disambiguationData":[TD([[makeQuery(id+"F15.imprint","IMPRINT",EDGE,{"derivedFrom":sQuery(id+"F15.wireOp",EDGE,"E114.bottom")}),-1.0]])]});
            extrude(context, id + "F17", {"entities" : qUnion([Q0]), "depth" : 10 * mm, "offsetDistance" : 25 * mm, "hasSecondDirection" : true, "secondDirectionOppositeDirection" : true, "secondDirectionDepth" : 15 * mm});
        }
        {
            var Q0;
            Q0=makeQuery(id+"F15.imprint","IMPRINT",FACE,{"disambiguationData":[TD([[makeQuery(id+"F15.imprint","IMPRINT",EDGE,{"derivedFrom":sQuery(id+"F15.wireOp",EDGE,"E114.bottom")}),-1.0]])]});
            var Q1;
            Q1=makeQuery(id+"F15.imprint","IMPRINT",FACE,{"disambiguationData":[TD([[makeQuery(id+"F15.imprint","IMPRINT",EDGE,{"derivedFrom":sQuery(id+"F15.wireOp",EDGE,"E115.bottom")}),-1.0]])]});
            extrude(context, id + "F18", {"entities" : qUnion([Q0, Q1]), "oppositeDirection" : true, "depth" : 45 * mm, "offsetDistance" : 25 * mm, "hasSecondDirection" : true, "secondDirectionOppositeDirection" : true, "secondDirectionDepth" : 40 * mm});
        }
        {
            var Q0;
            {var subQ9=sQuery(id+"F6.wireOp",EDGE,"E91.top");Q0=makeQuery(id+"F6.imprint","IMPRINT",FACE,{"disambiguationData":[TD([[makeQuery(id+"F6.imprint","IMPRINT",EDGE,{"derivedFrom":subQ9}),1.0]])]});}
            var Q1;
            Q1=makeQuery(id+"F6.imprint","IMPRINT",FACE,{"disambiguationData":[TD([[makeQuery(id+"F6.imprint","IMPRINT",EDGE,{"derivedFrom":sQuery(id+"F6.wireOp",EDGE,"E93.left")}),1.0]])]});
            var Q2;
            Q2=makeQuery(id+"F6.imprint","IMPRINT",FACE,{"disambiguationData":[TD([[makeQuery(id+"F6.imprint","IMPRINT",EDGE,{"derivedFrom":sQuery(id+"F6.wireOp",EDGE,"E105.bottom")}),-1.0]])]});
            var Q3;
            Q3=makeQuery(id+"F6.imprint","IMPRINT",FACE,{"disambiguationData":[TD([[makeQuery(id+"F6.imprint","IMPRINT",EDGE,{"derivedFrom":sQuery(id+"F6.wireOp",EDGE,"E102")}),1.0]])]});
            var Q4;
            Q4=makeQuery(id+"F6.imprint","IMPRINT",FACE,{"disambiguationData":[TD([[makeQuery(id+"F6.imprint","IMPRINT",EDGE,{"derivedFrom":sQuery(id+"F6.wireOp",EDGE,"E113")}),1.0]])]});
            var Q5;
            {var subQ2=sQuery(id+"F6.wireOp",EDGE,"E94");Q5=makeQuery(id+"F6.imprint","IMPRINT",FACE,{"disambiguationData":[TD([[makeQuery(id+"F6.imprint","IMPRINT",EDGE,{"derivedFrom":subQ2}),1.0]])]});}
            var Q6;
            {var subQ3=sQuery(id+"F6.wireOp",EDGE,"E100");Q6=makeQuery(id+"F6.imprint","IMPRINT",FACE,{"disambiguationData":[TD([[makeQuery(id+"F6.imprint","IMPRINT",EDGE,{"derivedFrom":subQ3}),1.0]])]});}
            var Q7;
            Q7=makeQuery(id+"F6.imprint","IMPRINT",FACE,{"disambiguationData":[TD([[makeQuery(id+"F6.imprint","IMPRINT",EDGE,{"derivedFrom":sQuery(id+"F6.wireOp",EDGE,"E108.bottom")}),-1.0]])]});
            var Q8;
            {var subQ3=sQuery(id+"F6.wireOp",EDGE,"E100");Q8=makeQuery(id+"F6.imprint","IMPRINT",FACE,{"disambiguationData":[TD([[makeQuery(id+"F6.imprint","IMPRINT",EDGE,{"derivedFrom":subQ3}),-1.0]])]});}
            extrude(context, id + "F19", {"entities" : qUnion([Q0, Q1, Q2, Q3, Q4, Q5, Q6, Q7, Q8]), "operationType" : NewBodyOperationType.REMOVE, "depth" : 1047 * mm, "offsetDistance" : 25 * mm});
        }
        {
            var Q0;
            Q0=makeQuery(id+"F6.imprint","IMPRINT",FACE,{"disambiguationData":[TD([[makeQuery(id+"F6.imprint","IMPRINT",EDGE,{"derivedFrom":sQuery(id+"F6.wireOp",EDGE,"E93.left")}),1.0]])]});
            var Q1;
            {var subQ3=sQuery(id+"F6.wireOp",EDGE,"E100");Q1=makeQuery(id+"F6.imprint","IMPRINT",FACE,{"disambiguationData":[TD([[makeQuery(id+"F6.imprint","IMPRINT",EDGE,{"derivedFrom":subQ3}),-1.0]])]});}
            var Q2;
            {var subQ3=sQuery(id+"F6.wireOp",EDGE,"E100");Q2=makeQuery(id+"F6.imprint","IMPRINT",FACE,{"disambiguationData":[TD([[makeQuery(id+"F6.imprint","IMPRINT",EDGE,{"derivedFrom":subQ3}),1.0]])]});}
            var Q3;
            Q3=makeQuery(id+"F6.imprint","IMPRINT",FACE,{"disambiguationData":[TD([[makeQuery(id+"F6.imprint","IMPRINT",EDGE,{"derivedFrom":sQuery(id+"F6.wireOp",EDGE,"E102")}),1.0]])]});
            var Q4;
            {var subQ2=sQuery(id+"F6.wireOp",EDGE,"E94");Q4=makeQuery(id+"F6.imprint","IMPRINT",FACE,{"disambiguationData":[TD([[makeQuery(id+"F6.imprint","IMPRINT",EDGE,{"derivedFrom":subQ2}),1.0]])]});}
            var Q5;
            {var subQ9=sQuery(id+"F6.wireOp",EDGE,"E91.top");Q5=makeQuery(id+"F6.imprint","IMPRINT",FACE,{"disambiguationData":[TD([[makeQuery(id+"F6.imprint","IMPRINT",EDGE,{"derivedFrom":subQ9}),1.0]])]});}
            extrude(context, id + "F20", {"entities" : qUnion([Q0, Q1, Q2, Q3, Q4, Q5]), "operationType" : NewBodyOperationType.ADD, "depth" : 930 * mm, "offsetDistance" : 25 * mm, "hasSecondDirection" : true, "secondDirectionOppositeDirection" : false, "secondDirectionDepth" : 900 * mm});
        }
        {
            var Q0;
            Q0=makeQuery(id+"F6.imprint","IMPRINT",FACE,{"disambiguationData":[TD([[makeQuery(id+"F6.imprint","IMPRINT",EDGE,{"derivedFrom":sQuery(id+"F6.wireOp",EDGE,"E93.left")}),1.0]])]});
            var Q1;
            Q1=makeQuery(id+"F6.imprint","IMPRINT",FACE,{"disambiguationData":[TD([[makeQuery(id+"F6.imprint","IMPRINT",EDGE,{"derivedFrom":sQuery(id+"F6.wireOp",EDGE,"E105.bottom")}),-1.0]])]});
            var Q2;
            Q2=makeQuery(id+"F6.imprint","IMPRINT",FACE,{"disambiguationData":[TD([[makeQuery(id+"F6.imprint","IMPRINT",EDGE,{"derivedFrom":sQuery(id+"F6.wireOp",EDGE,"E108.bottom")}),-1.0]])]});
            var Q3;
            Q3=makeQuery(id+"F6.imprint","IMPRINT",FACE,{"disambiguationData":[TD([[makeQuery(id+"F6.imprint","IMPRINT",EDGE,{"derivedFrom":sQuery(id+"F6.wireOp",EDGE,"E113")}),1.0]])]});
            extrude(context, id + "F21", {"entities" : qUnion([Q0, Q1, Q2, Q3]), "depth" : 950 * mm, "offsetDistance" : 25 * mm, "hasSecondDirection" : true, "secondDirectionOppositeDirection" : false, "secondDirectionDepth" : 930 * mm});
        }
        {
            var Q0;
            Q0=makeQuery(id+"F21.opExtrude","SWEPT_EDGE",EDGE,{"disambiguationData":[OSD([sQuery(id+"F6.wireOp",EDGE,"E93.left"),sQuery(id+"F6.wireOp",EDGE,"E96")])]});
            var Q1;
            Q1=makeQuery(id+"F21.opExtrude","SWEPT_EDGE",EDGE,{"disambiguationData":[OSD([sQuery(id+"F6.wireOp",EDGE,"E93.left"),sQuery(id+"F6.wireOp",EDGE,"E101")])]});
            var Q2;
            Q2=makeQuery(id+"F21.opExtrude","SWEPT_EDGE",EDGE,{"disambiguationData":[OSD([sQuery(id+"F6.wireOp",EDGE,"E102"),sQuery(id+"F6.wireOp",EDGE,"E103"),sQuery(id+"F6.wireOp",EDGE,"E104")])]});
            var Q3;
            Q3=makeQuery(id+"F21.opExtrude","SWEPT_EDGE",EDGE,{"disambiguationData":[OSD([sQuery(id+"F6.wireOp",EDGE,"E93.bottom"),sQuery(id+"F6.wireOp",EDGE,"E98"),sQuery(id+"F6.wireOp",EDGE,"E99")])]});
            var Q4;
            Q4=makeQuery(id+"F21.opExtrude","SWEPT_EDGE",EDGE,{"disambiguationData":[OSD([sQuery(id+"F6.wireOp",EDGE,"E101"),sQuery(id+"F6.wireOp",EDGE,"E102"),sQuery(id+"F6.wireOp",EDGE,"E104")])]});
            var Q5;
            Q5=makeQuery(id+"F21.opExtrude","SWEPT_EDGE",EDGE,{"disambiguationData":[OSD([sQuery(id+"F6.wireOp",EDGE,"E93.right"),sQuery(id+"F6.wireOp",EDGE,"E103")])]});
            var Q6;
            Q6=makeQuery(id+"F21.opExtrude","SWEPT_EDGE",EDGE,{"disambiguationData":[OSD([sQuery(id+"F6.wireOp",EDGE,"E93.right"),sQuery(id+"F6.wireOp",EDGE,"E98")])]});
            var Q7;
            Q7=makeQuery(id+"F21.opExtrude","SWEPT_EDGE",EDGE,{"disambiguationData":[OSD([sQuery(id+"F6.wireOp",EDGE,"E93.bottom"),sQuery(id+"F6.wireOp",EDGE,"E96"),sQuery(id+"F6.wireOp",EDGE,"E99")])]});
            fillet(context, id + "F22", {"entities" : qUnion([Q0, Q1, Q2, Q3, Q4, Q5, Q6, Q7]), "radius" : 13 * mm, "tangentPropagation" : true, "allowEdgeOverflow" : false});
        }
        {
            var Q0;
            Q0=makeQuery(id+"F19.boolean.opBoolean","COPY",EDGE,{"derivedFrom":makeQuery(id+"F19.opExtrude","SWEPT_EDGE",EDGE,{"disambiguationData":[OSD([sQuery(id+"F6.wireOp",EDGE,"E91.top"),sQuery(id+"F6.wireOp",EDGE,"E91.left")])]})});
            var Q1;
            Q1=makeQuery(id+"F19.boolean.opBoolean","COPY",EDGE,{"derivedFrom":makeQuery(id+"F19.opExtrude","SWEPT_EDGE",EDGE,{"disambiguationData":[OSD([sQuery(id+"F6.wireOp",EDGE,"E91.bottom"),sQuery(id+"F6.wireOp",EDGE,"E91.left")])]})});
            var Q2;
            Q2=makeQuery(id+"F19.boolean.opBoolean","COPY",EDGE,{"derivedFrom":makeQuery(id+"F19.opExtrude","SWEPT_EDGE",EDGE,{"disambiguationData":[OSD([sQuery(id+"F6.wireOp",EDGE,"E91.bottom"),sQuery(id+"F6.wireOp",EDGE,"E91.right")])]})});
            var Q3;
            Q3=makeQuery(id+"F19.boolean.opBoolean","COPY",EDGE,{"derivedFrom":makeQuery(id+"F19.opExtrude","SWEPT_EDGE",EDGE,{"disambiguationData":[OSD([sQuery(id+"F6.wireOp",EDGE,"E91.top"),sQuery(id+"F6.wireOp",EDGE,"E91.right")])]})});
            fillet(context, id + "F23", {"entities" : qUnion([Q0, Q1, Q2, Q3]), "radius" : 10 * mm, "tangentPropagation" : true, "allowEdgeOverflow" : false});
        }
        {
            var Q0;
            Q0=makeQuery(id+"F19.boolean.opBoolean","INTERSECT",EDGE,{"derivedFrom":[makeQuery(id+"F1.opExtrude","CAP_FACE",FACE,{"disambiguationData":[OSD([sQuery(id+"F0.wireOp",EDGE,"E0"),sQuery(id+"F0.wireOp",EDGE,"E1"),sQuery(id+"F0.wireOp",EDGE,"E2"),sQuery(id+"F0.wireOp",EDGE,"E3"),sQuery(id+"F0.wireOp",EDGE,"E4"),sQuery(id+"F0.wireOp",EDGE,"E5")])],"isStart":false}),makeQuery(id+"F19.opExtrude","SWEPT_FACE",FACE,{"disambiguationData":[OSD([sQuery(id+"F6.wireOp",EDGE,"E91.top")])]})]});
            var Q1;
            Q1=makeQuery(id+"F21.opExtrude","CAP_FACE",FACE,{"disambiguationData":[OSD([sQuery(id+"F6.wireOp",EDGE,"E93.left"),sQuery(id+"F6.wireOp",EDGE,"E93.right"),sQuery(id+"F6.wireOp",EDGE,"E96"),sQuery(id+"F6.wireOp",EDGE,"E98"),sQuery(id+"F6.wireOp",EDGE,"E99"),sQuery(id+"F6.wireOp",EDGE,"E101"),sQuery(id+"F6.wireOp",EDGE,"E103"),sQuery(id+"F6.wireOp",EDGE,"E104")])],"isStart":false});
            chamfer(context, id + "F24", {"entities" : qUnion([Q0, Q1]), "width" : 3 * mm, "tangentPropagation" : true});
        }
    });
